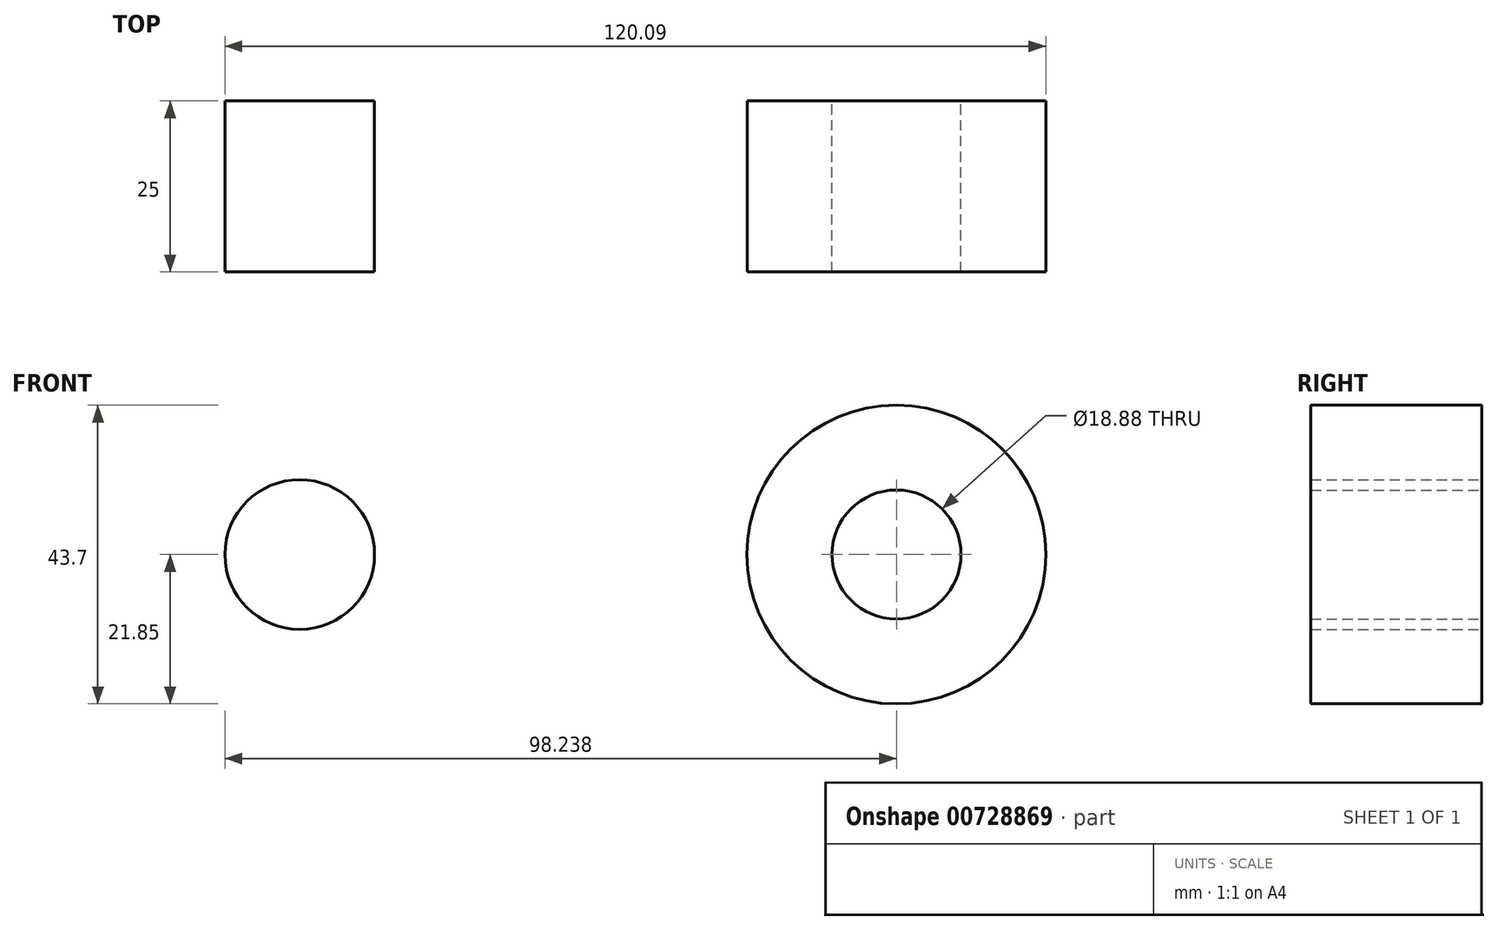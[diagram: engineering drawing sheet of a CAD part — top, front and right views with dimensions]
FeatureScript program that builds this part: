
annotation { "Feature Type Name" : "Feature", "Feature Type Description" : "" }
export const myFeature = defineFeature(function(context is Context, id is Id, definition is map)
    precondition{}
    {
        {
            var Q0;
            Q0=qCreatedBy(makeId("Front.planeOp"),FACE);
            var sketch = newSketch(context, id + "F0", { "sketchPlane" : qUnion([Q0])});
            skCircle(sketch, "E0", {"center": v(40.25, 0) * mm, "radius": 21.85 * mm});
            skCircle(sketch, "E1", {"center": v(40.25, 0) * mm, "radius": 9.44 * mm});
            skCircle(sketch, "E2", {"center": v(-47.04, 0) * mm, "radius": 10.95 * mm});
            skSolve(sketch);
        }
        {
            var Q0;
            Q0 = qSketchRegion(id + "F0", true);
            extrude(context, id + "F1", {"entities" : qUnion([Q0]), "depth" : 25 * mm, "offsetDistance" : 25 * mm});
        }
    });
